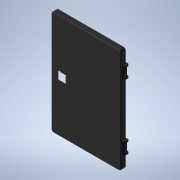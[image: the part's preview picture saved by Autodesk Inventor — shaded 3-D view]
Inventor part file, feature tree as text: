
AUTODESK INVENTOR PART (.ipt)
format: ipt  version: 2021 (Build 250183000, 183)  size: 390,144 bytes
history: native  units: mm
features: other x28, sketch x20, extrude x11, revolve x9, thread x1
ambient origin geometry x8: Origin, YZ Plane, XZ Plane, XY Plane, X Axis, Y Axis, Z Axis, Center Point
bodies: Solid1 (feature_tree)
feature tree (69):
  extrude  "Extrusion1"  Depth=286.0mm TaperAngle=0.0deg
  extrude  "Extrusion2"  TaperAngle=90.0deg  [1 undecoded]
  revolve  "Revolution1"  Angle=90.0deg
  revolve  "Revolution2"  Angle=90.0deg
  revolve  "Revolution3"  Angle=90.0deg
  revolve  "Revolution4"  [1 undecoded]
  extrude  "Extrusion3"  Depth=188.0mm TaperAngle=0.0deg
  revolve  "Revolution5"  Angle=360.0deg
  revolve  "Revolution6"  [1 undecoded]
  revolve  "Revolution7"  [1 undecoded]
  revolve  "Revolution8"  [1 undecoded]
  extrude  "Extrusion4"  [1 undecoded]
  extrude  "Extrusion5"  [1 undecoded]
  extrude  "Extrusion6"  [1 undecoded]
  extrude  "Extrusion7"  [1 undecoded]
  revolve  "Revolution9"  [1 undecoded]
  thread  "Thread1"  [1 undecoded]
  extrude  "Extrusion8"  [1 undecoded]
  extrude  "Extrusion9"  [1 undecoded]
  extrude  "Extrusion10"  [1 undecoded]
  extrude  "Extrusion11"  [1 undecoded]
  other  "DECKEL_XY"
  other  "DECKEL_YZ"
  other  "DECKEL_ZX"
  other  "DECKEL_X"
  other  "DECKEL_Y"
  other  "DECKEL_Z"
  other  "DECKEL_Center"
  other  "VB_XY"
  other  "VB_YZ"
  other  "VB_ZX"
  other  "VB_X"
  other  "VB_Y"
  other  "VB_Z"
  other  "VB_Center"
  other  "to_HINGE_XY"
  other  "to_HINGE_YZ"
  other  "to_HINGE_ZX"
  other  "to_HINGE_X"
  other  "to_HINGE_Y"
  other  "to_HINGE_Z"
  other  "to_HINGE_Center"
  other  "to_HINGE_1_XY"
  other  "to_HINGE_1_YZ"
  other  "to_HINGE_1_ZX"
  other  "to_HINGE_1_X"
  other  "to_HINGE_1_Y"
  other  "to_HINGE_1_Z"
  other  "to_HINGE_1_Center"
  sketch  "Skizze_2"  dims[d4=90.0deg d5=90.0deg]
  sketch  "Skizze_4"  dims[d8=176.5mm d9=0.0mm d10=90.0deg]
  sketch  "Skizze_5"  dims[d13=90.0deg d14=276.5mm d15=0.0mm]
  sketch  "Skizze_6"  dims[d20=1.25mm d21=0.0mm d22=360.0deg]
  sketch  "Skizze_7"  dims[d27=35.0mm d28=0.0mm d29=25.0mm d30=0.0mm]
  sketch  "Skizze_8"  dims[d31=25.0mm d32=0.0mm d33=0.0mm d34=0.0mm]
  sketch  "Skizze_29"
  sketch  "Skizze_30"
  sketch  "Skizze_31"
  sketch  "Skizze_32"
  sketch  "Skizze_33"
  sketch  "Skizze_34"
  sketch  "Sketch_5"  dims[d16=288.0mm d17=0.0mm d18=188.0mm d19=0.0mm]
  sketch  "Sketch_6"  dims[d23=7.1865mm d24=0.0mm d25=35.0mm d26=0.0mm]
  sketch  "Sketch_3"  dims[d6=90.0deg d7=90.0deg]
  sketch  "Sketch_1"  dims[d0=186.0mm d1=0.0mm d2=286.0mm d3=0.0mm]
  sketch  "Sketch_4"  dims[d11=90.0deg d12=90.0deg]
  sketch  "Sketch_10"
  sketch  "Sketch_9"
  sketch  "Sketch_11"
note: 15 required parameter values undecoded (feature->parameter linkage not recoverable at this tier; creation-order binding heuristic only, values carry confidence <= 0.55)